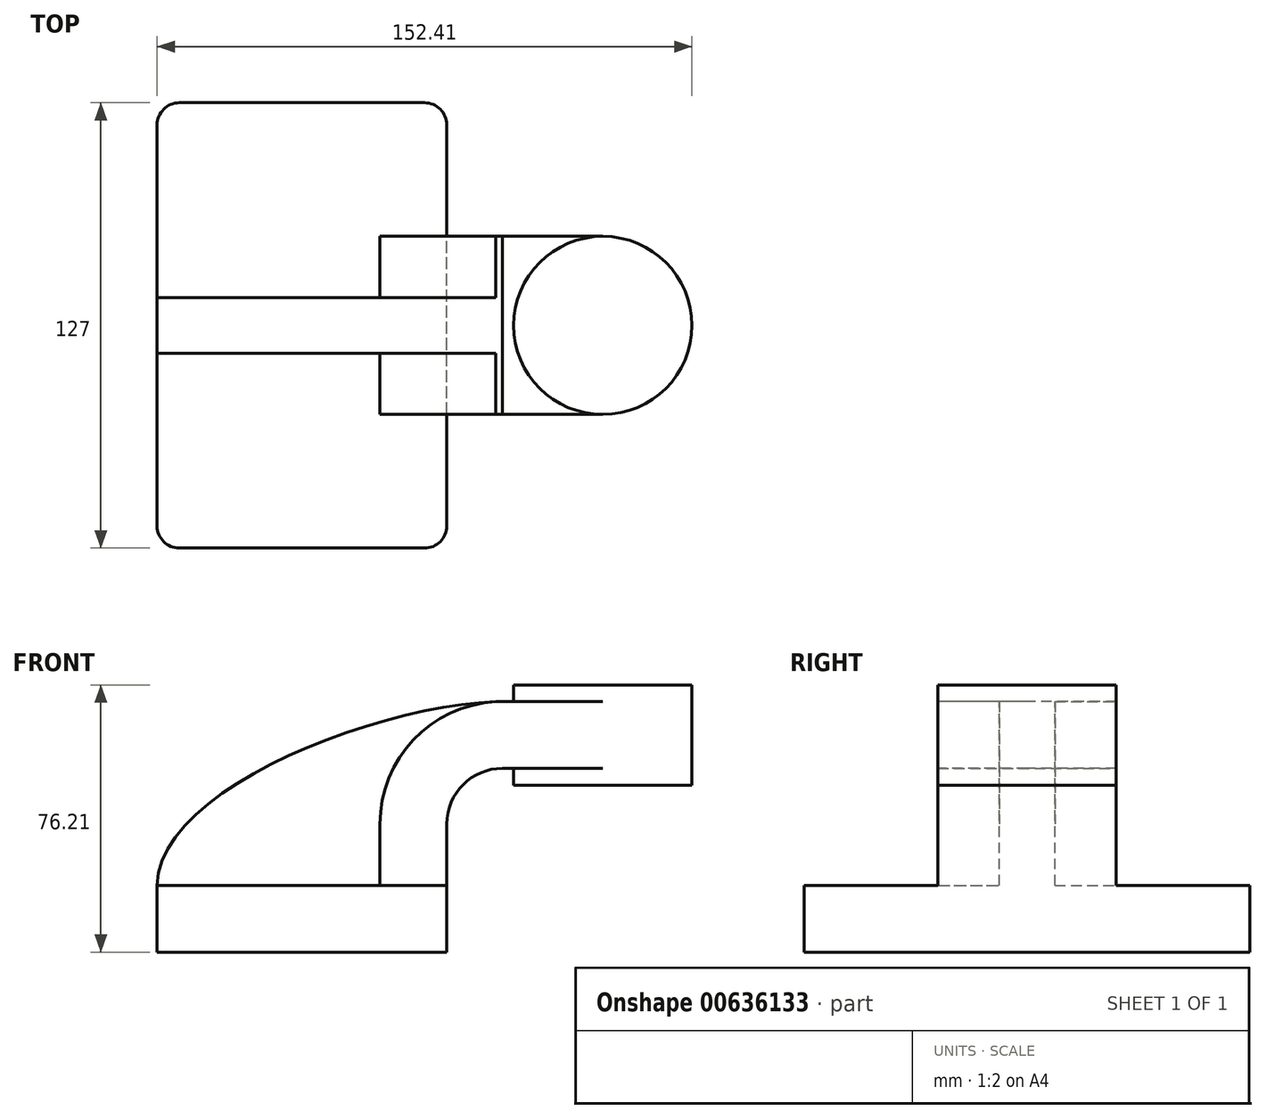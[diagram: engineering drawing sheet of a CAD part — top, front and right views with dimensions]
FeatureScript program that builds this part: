
annotation { "Feature Type Name" : "Feature", "Feature Type Description" : "" }
export const myFeature = defineFeature(function(context is Context, id is Id, definition is map)
    precondition{}
    {
        {
            var Q0;
            Q0=qCreatedBy(makeId("Front.planeOp"),FACE);
            var sketch = newSketch(context, id + "F0", { "sketchPlane" : qUnion([Q0])});
            skLineSegment(sketch, "E0.bottom", {"start": v(-41.28, -9.52) * mm, "end": v(41.28, -9.52) * mm});
            skLineSegment(sketch, "E0.top", {"start": v(-41.28, 9.52) * mm, "end": v(41.27, 9.52) * mm});
            skLineSegment(sketch, "E0.left", {"start": v(-41.28, -9.52) * mm, "end": v(-41.28, 9.53) * mm});
            skLineSegment(sketch, "E0.right", {"start": v(41.27, -9.52) * mm, "end": v(41.27, 9.53) * mm});
            skPoint(sketch, "E0.middle", {"position": v(0, 0) * mm});
            skLineSegment(sketch, "E1.bottom", {"start": v(60.32, 38.1) * mm, "end": v(111.12, 38.1) * mm});
            skLineSegment(sketch, "E1.top", {"start": v(60.32, 66.68) * mm, "end": v(111.12, 66.68) * mm});
            skLineSegment(sketch, "E1.right", {"start": v(111.12, 38.1) * mm, "end": v(111.12, 66.68) * mm});
            skPoint(sketch, "E1.middle", {"position": v(85.72, 52.39) * mm});
            skLineSegment(sketch, "E2", {"start": v(60.32, 66.68) * mm, "end": v(60.32, 38.1) * mm});
            skLineSegment(sketch, "E3", {"start": v(41.27, 9.53) * mm, "end": v(41.27, 27) * mm});
            skArc(sketch, "E4", {"start": v(41.27, 27) * mm, "mid": v(45.92, 38.23) * mm, "end": v(57.15, 42.88) * mm});
            skLineSegment(sketch, "E5", {"start": v(57.15, 42.88) * mm, "end": v(85.72, 42.88) * mm});
            skLineSegment(sketch, "E6.0", {"start": v(57.15, 61.93) * mm, "end": v(85.72, 61.93) * mm});
            skArc(sketch, "E6.1", {"start": v(22.22, 27) * mm, "mid": v(32.45, 51.7) * mm, "end": v(57.15, 61.93) * mm});
            skLineSegment(sketch, "E6.2", {"start": v(22.22, 9.53) * mm, "end": v(22.22, 27) * mm});
            skLineSegment(sketch, "E7", {"start": v(85.72, 38.1) * mm, "end": v(85.72, 66.68) * mm});
            skFitSpline(sketch, "E8", {"points": [v(-41.28, 9.53) * mm, v(57.15, 61.93) * mm], "startDerivative": vector(0.34, 82.22) * mm, "endDerivative": vector(105.65, 1.69) * mm});
            skSolve(sketch);
        }
        {
            var Q0;
            Q0=makeQuery(id+"F0.imprint","IMPRINT",FACE,{"disambiguationData":[TD([[makeQuery(id+"F0.imprint","IMPRINT",EDGE,{"derivedFrom":sQuery(id+"F0.wireOp",EDGE,"E0.bottom")}),1.0]])]});
            extrude(context, id + "F1", {"entities" : qUnion([Q0]), "endBound" : BoundingType.SYMMETRIC, "depth" : 127 * mm, "offsetDistance" : 25.4 * mm});
        }
        {
            var Q0;
            {var subQ1=sQuery(id+"F0.wireOp",EDGE,"E3");Q0=makeQuery(id+"F0.imprint","IMPRINT",FACE,{"disambiguationData":[TD([[makeQuery(id+"F0.imprint","IMPRINT",EDGE,{"derivedFrom":subQ1}),1.0]])]});}
            var Q1;
            {var subQ0=sQuery(id+"F0.wireOp",EDGE,"E6.0");var subQ1=sQuery(id+"F0.wireOp",EDGE,"E2");var subQ2=makeQuery(id+"F0.imprint","INTERSECT",VERTEX,{"derivedFrom":[subQ1,subQ0]});Q1=makeQuery(id+"F0.imprint","IMPRINT",FACE,{"disambiguationData":[TD([[makeQuery(id+"F0.imprint","IMPRINT",EDGE,{"disambiguationData":[TD([[subQ2,-1.0]])],"derivedFrom":subQ1}),1.0]])]});}
            extrude(context, id + "F2", {"entities" : qUnion([Q0, Q1]), "operationType" : NewBodyOperationType.ADD, "endBound" : BoundingType.SYMMETRIC, "depth" : 50.8 * mm, "offsetDistance" : 25.4 * mm});
        }
        {
            var Q0;
            {var subQ3=sQuery(id+"F0.wireOp",EDGE,"E6.2");Q0=makeQuery(id+"F0.imprint","IMPRINT",FACE,{"disambiguationData":[TD([[makeQuery(id+"F0.imprint","IMPRINT",EDGE,{"derivedFrom":subQ3}),1.0]])]});}
            extrude(context, id + "F3", {"entities" : qUnion([Q0]), "operationType" : NewBodyOperationType.ADD, "endBound" : BoundingType.SYMMETRIC, "depth" : 15.88 * mm, "offsetDistance" : 25.4 * mm});
        }
        {
            var Q0;
            {var subQ4=sQuery(id+"F0.wireOp",EDGE,"E1.right");Q0=makeQuery(id+"F0.imprint","IMPRINT",FACE,{"disambiguationData":[TD([[makeQuery(id+"F0.imprint","IMPRINT",EDGE,{"derivedFrom":subQ4}),1.0]])]});}
            var Q1;
            Q1=sQuery(id+"F0.wireOp",EDGE,"E7");
            revolve(context, id + "F4", {"operationType" : NewBodyOperationType.ADD, "entities" : qUnion([Q0]), "axis" : qUnion([Q1]), "revolveType" : RevolveType.FULL});
        }
        {
            var Q0;
            Q0=makeQuery(id+"F1.opExtrude","CAP_EDGE",EDGE,{"disambiguationData":[OSD([sQuery(id+"F0.wireOp",EDGE,"E0.right")])],"isStart":false});
            var Q1;
            Q1=makeQuery(id+"F1.opExtrude","CAP_EDGE",EDGE,{"disambiguationData":[OSD([sQuery(id+"F0.wireOp",EDGE,"E0.left")])],"isStart":false});
            var Q2;
            Q2=makeQuery(id+"F1.opExtrude","CAP_EDGE",EDGE,{"disambiguationData":[OSD([sQuery(id+"F0.wireOp",EDGE,"E0.right")])],"isStart":true});
            var Q3;
            Q3=makeQuery(id+"F1.opExtrude","CAP_EDGE",EDGE,{"disambiguationData":[OSD([sQuery(id+"F0.wireOp",EDGE,"E0.left")])],"isStart":true});
            fillet(context, id + "F5", {"entities" : qUnion([Q0, Q1, Q2, Q3]), "radius" : 6.35 * mm, "tangentPropagation" : true, "allowEdgeOverflow" : false});
        }
    });
